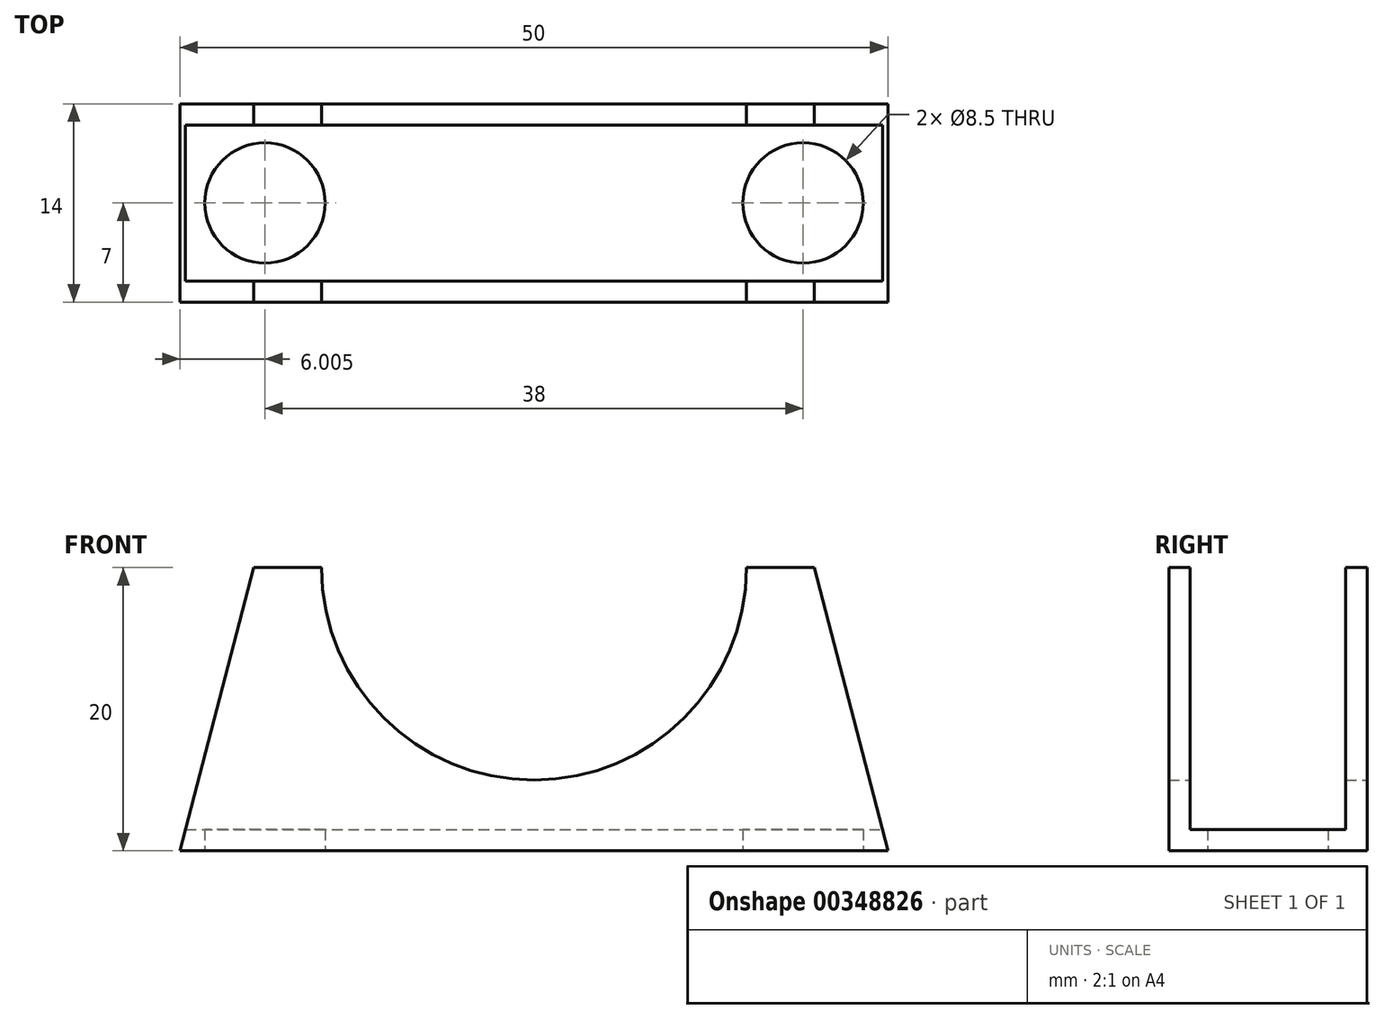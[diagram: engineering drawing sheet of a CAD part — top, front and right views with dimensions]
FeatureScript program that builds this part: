
annotation { "Feature Type Name" : "Feature", "Feature Type Description" : "" }
export const myFeature = defineFeature(function(context is Context, id is Id, definition is map)
    precondition{}
    {
        {
            var Q0;
            Q0=qCreatedBy(makeId("Front.planeOp"),FACE);
            var sketch = newSketch(context, id + "F0", { "sketchPlane" : qUnion([Q0])});
            skLineSegment(sketch, "E0", {"start": v(-59.09, 2.78) * mm, "end": v(-9.09, 2.78) * mm});
            skLineSegment(sketch, "E1", {"start": v(-9.09, 2.78) * mm, "end": v(-14.29, 22.78) * mm});
            skLineSegment(sketch, "E2", {"start": v(-14.29, 22.78) * mm, "end": v(-19.09, 22.78) * mm});
            skLineSegment(sketch, "E3", {"start": v(-59.09, 2.78) * mm, "end": v(-53.88, 22.78) * mm});
            skLineSegment(sketch, "E4", {"start": v(-53.88, 22.78) * mm, "end": v(-49.09, 22.78) * mm});
            skArc(sketch, "E5", {"start": v(-49.09, 22.78) * mm, "mid": v(-34.09, 7.78) * mm, "end": v(-19.09, 22.78) * mm});
            skLineSegment(sketch, "E6", {"start": v(-34.09, 22.78) * mm, "end": v(-34.09, -12.93) * mm, "construction": true});
            skSolve(sketch);
        }
        {
            var Q0;
            Q0=qSketchRegion(id+"F0",true);
            extrude(context, id + "F1", {"entities" : qUnion([Q0]), "depth" : 14 * mm});
        }
        {
            var Q0;
            Q0=makeQuery(id+"F1.opExtrude","SWEPT_FACE",FACE,{"disambiguationData":[OSD([sQuery(id+"F0.wireOp",EDGE,"E3")])]});
            var Q1;
            Q1=makeQuery(id+"F1.opExtrude","SWEPT_FACE",FACE,{"disambiguationData":[OSD([sQuery(id+"F0.wireOp",EDGE,"E4")])]});
            var Q2;
            Q2=makeQuery(id+"F1.opExtrude","SWEPT_FACE",FACE,{"disambiguationData":[OSD([sQuery(id+"F0.wireOp",EDGE,"E5")])]});
            var Q3;
            Q3=makeQuery(id+"F1.opExtrude","SWEPT_FACE",FACE,{"disambiguationData":[OSD([sQuery(id+"F0.wireOp",EDGE,"E2")])]});
            var Q4;
            Q4=makeQuery(id+"F1.opExtrude","SWEPT_FACE",FACE,{"disambiguationData":[OSD([sQuery(id+"F0.wireOp",EDGE,"E1")])]});
            shell(context, id + "F2", {"entities" : qUnion([Q0, Q1, Q2, Q3, Q4]), "thickness" : 1.5 * mm});
        }
        {
            var Q0;
            Q0=makeQuery(id+"F1.opExtrude","SWEPT_FACE",FACE,{"disambiguationData":[OSD([sQuery(id+"F0.wireOp",EDGE,"E0")])]});
            var sketch = newSketch(context, id + "F3", { "sketchPlane" : qUnion([Q0])});
            skPoint(sketch, "E7", {"position": v(-53.09, 7) * mm});
            skPoint(sketch, "E8", {"position": v(-15.09, 7) * mm});
            skSolve(sketch);
        }
        {
            var Q0;
            Q0=sQuery(id+"F3.wireOp",VERTEX,"E7");
            var Q1;
            Q1=makeQuery(id+"F1.opExtrude","SWEPT_BODY",BODY,{"disambiguationData":[OSD([sQuery(id+"F0.wireOp",EDGE,"E0"),sQuery(id+"F0.wireOp",EDGE,"E1"),sQuery(id+"F0.wireOp",EDGE,"E2"),sQuery(id+"F0.wireOp",EDGE,"E3"),sQuery(id+"F0.wireOp",EDGE,"E4"),sQuery(id+"F0.wireOp",EDGE,"E5")])]});
            hole(context, id + "F4", {"style" : HoleStyle.SIMPLE, "endStyle" : HoleEndStyle.THROUGH, "holeDiameter" : 8.5 * mm, "isTappedThrough" : true, "tappedDepth" : 12 * mm, "tapClearance" : 3, "locations" : qUnion([Q0]), "scope" : qUnion([Q1])});
        }
        {
            var Q0;
            Q0=sQuery(id+"F3.wireOp",VERTEX,"E8");
            var Q1;
            Q1=makeQuery(id+"F1.opExtrude","SWEPT_BODY",BODY,{"disambiguationData":[OSD([sQuery(id+"F0.wireOp",EDGE,"E0"),sQuery(id+"F0.wireOp",EDGE,"E1"),sQuery(id+"F0.wireOp",EDGE,"E2"),sQuery(id+"F0.wireOp",EDGE,"E3"),sQuery(id+"F0.wireOp",EDGE,"E4"),sQuery(id+"F0.wireOp",EDGE,"E5")])]});
            hole(context, id + "F5", {"style" : HoleStyle.SIMPLE, "endStyle" : HoleEndStyle.THROUGH, "holeDiameter" : 8.5 * mm, "isTappedThrough" : true, "tappedDepth" : 12 * mm, "tapClearance" : 3, "locations" : qUnion([Q0]), "scope" : qUnion([Q1])});
        }
    });
